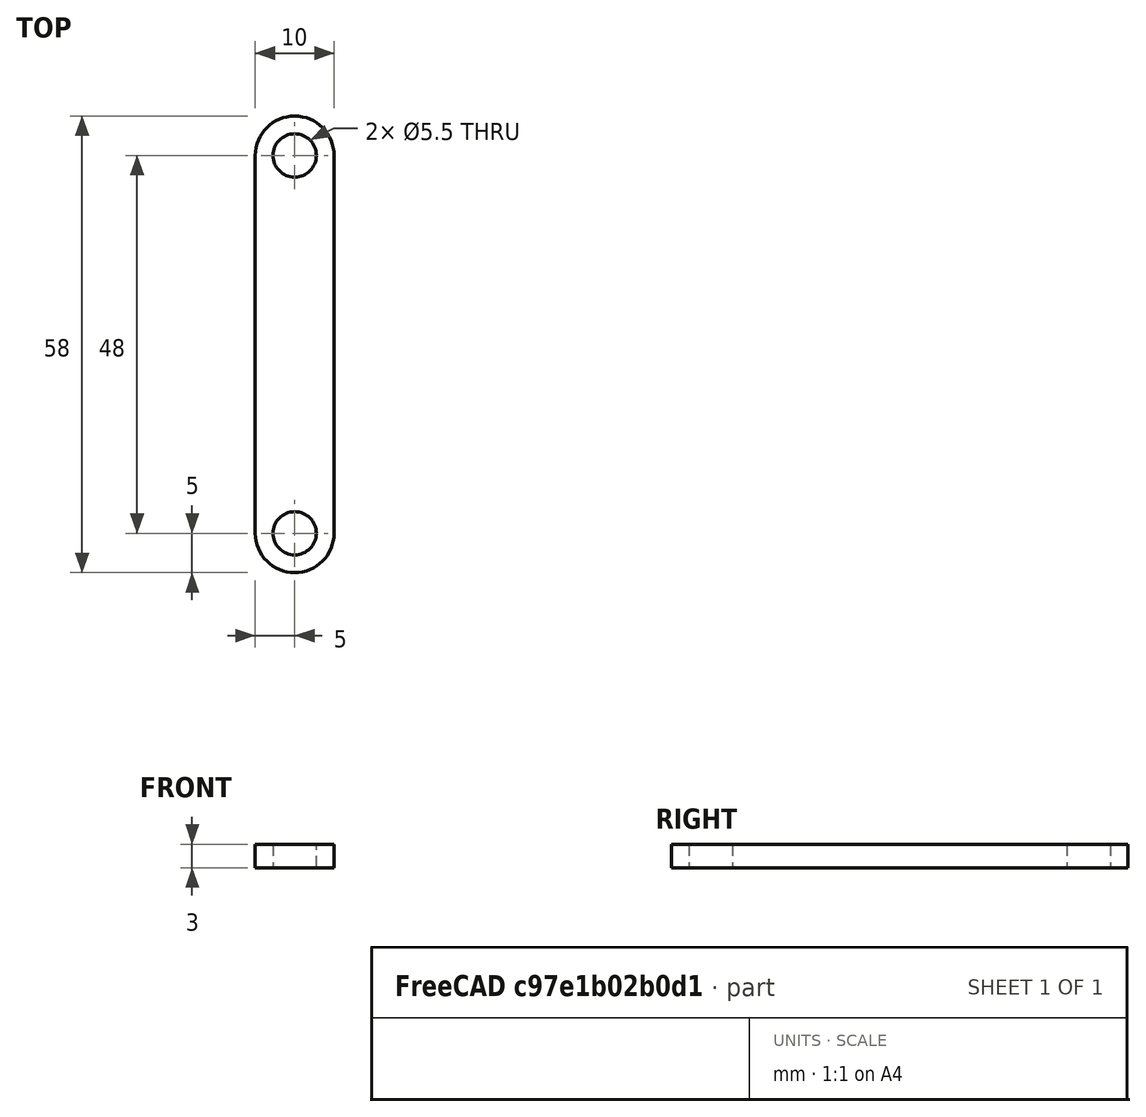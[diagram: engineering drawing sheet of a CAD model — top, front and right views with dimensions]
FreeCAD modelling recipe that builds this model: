
FCSTD DOCUMENT  (FreeCAD 0.19R24276 (Git))
Label: Lens_holder_Part_3
License: All rights reserved
LicenseURL: http://en.wikipedia.org/wiki/All_rights_reserved
objects: Sketcher::SketchObject×1, PartDesign::Pad×1, PartDesign::Body×1
note: 4 computed .brp shape members not serialized (recipe doc carries the construction recipe); baked Part::Feature solids carry a one-line shape summary decoded from their .brp

FEATURE [Sketcher::SketchObject] Sketch
  FullyConstrained = true
  MapMode = 5
  Support = -> [XY_Plane]
  sketch-geometry (6):
    g0: Circle CenterX=0 CenterY=48 CenterZ=0 NormalX=0 NormalY=0 NormalZ=1 AngleXU=0 Radius=2.75
    g1: Circle CenterX=0 CenterY=0 CenterZ=0 NormalX=0 NormalY=0 NormalZ=1 AngleXU=0 Radius=2.75
    g2: ArcOfCircle CenterX=0 CenterY=48 CenterZ=0 NormalX=0 NormalY=0 NormalZ=1 AngleXU=0 Radius=5 StartAngle=-4.4e-15 EndAngle=3.14159
    g3: ArcOfCircle CenterX=0 CenterY=0 CenterZ=0 NormalX=0 NormalY=0 NormalZ=1 AngleXU=0 Radius=5 StartAngle=3.14159 EndAngle=6.28319
    g4: LineSegment StartX=-5 StartY=48 StartZ=0 EndX=-5 EndY=0 EndZ=0
    g5: LineSegment StartX=5 StartY=48 StartZ=0 EndX=5 EndY=-2.13e-14 EndZ=0
  constraints (13):
    c: PointOnObject(g0,g-2)
    c: Coincident(g1,g-1)
    c: DistanceY(g1,g0) = 48
    c: Diameter(g1) = 5.5
    c: Equal(g1,g0)
    c: Tangent(g2,g5) = 1.5708
    c: Tangent(g2,g4) = -1.5708
    c: Tangent(g4,g3) = -1.5708
    c: Tangent(g5,g3) = 1.5708
    c: Vertical(g4)
    c: Coincident(g2,g0)
    c: Coincident(g3,g1)
    c: Diameter(g3) = 10
FEATURE [PartDesign::Pad] Pad
  Direction = (1,1,1)
  Length = 3
  Length2 = 100
  Profile = -> Sketch
  Type = 0
FEATURE [PartDesign::Body] Body
  Group = -> [Sketch,Pad]
  Origin = -> Origin
  Tip = -> Pad
